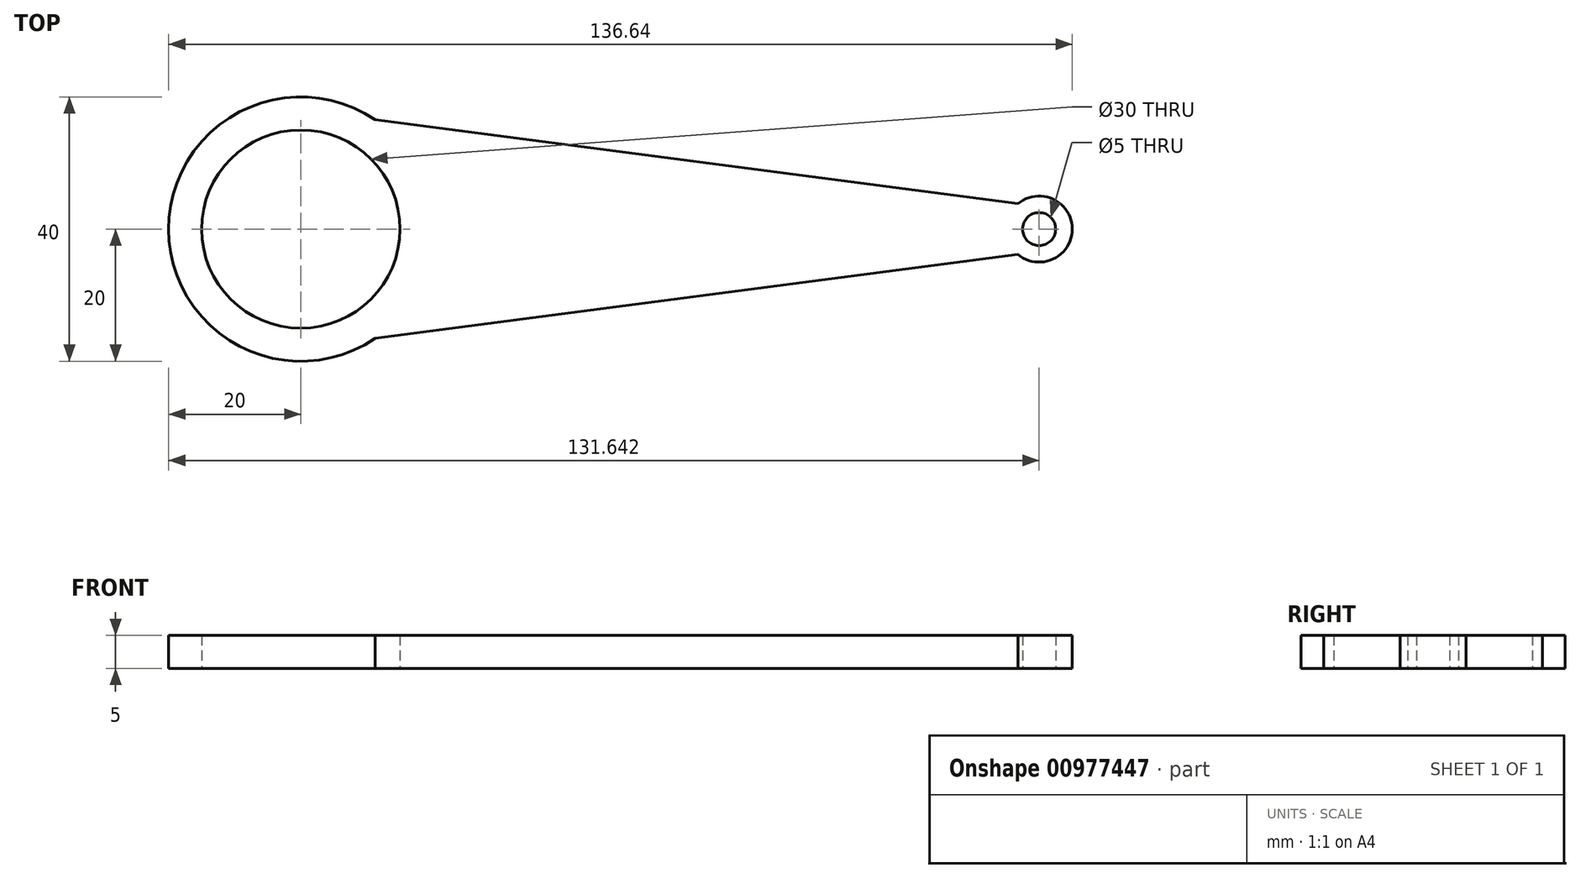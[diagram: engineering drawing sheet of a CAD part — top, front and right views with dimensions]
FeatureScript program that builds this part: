
annotation { "Feature Type Name" : "Feature", "Feature Type Description" : "" }
export const myFeature = defineFeature(function(context is Context, id is Id, definition is map)
    precondition{}
    {
        {
            var Q0;
            Q0=qCreatedBy(makeId("Top.planeOp"),FACE);
            var sketch = newSketch(context, id + "F0", { "sketchPlane" : qUnion([Q0])});
            skCircle(sketch, "E0", {"center": v(-131.43, 0) * mm, "radius": 15 * mm});
            skCircle(sketch, "E1", {"center": v(-19.79, 0) * mm, "radius": 2.5 * mm});
            skCircle(sketch, "E2", {"center": v(-131.43, 0) * mm, "radius": 20 * mm});
            skCircle(sketch, "E3", {"center": v(-19.79, 0) * mm, "radius": 5 * mm});
            skLineSegment(sketch, "E4", {"start": v(-131.43, 0) * mm, "end": v(-19.79, 0) * mm, "construction": true});
            skLineSegment(sketch, "E5", {"start": v(-120.18, 32.86) * mm, "end": v(-120.18, -33.62) * mm, "construction": true});
            skLineSegment(sketch, "E6", {"start": v(-22.99, 9.9) * mm, "end": v(-22.99, -15.53) * mm, "construction": true});
            skLineSegment(sketch, "E7", {"start": v(-120.18, 16.53) * mm, "end": v(-22.99, 3.84) * mm});
            skLineSegment(sketch, "E8", {"start": v(-22.99, -3.84) * mm, "end": v(-120.18, -16.53) * mm});
            skSolve(sketch);
        }
        {
            var Q0;
            Q0=makeQuery(id+"F0.imprint","IMPRINT",FACE,{"disambiguationData":[TD([[makeQuery(id+"F0.imprint","IMPRINT",EDGE,{"derivedFrom":sQuery(id+"F0.wireOp",EDGE,"E0")}),-1.0]])]});
            var Q1;
            {var subQ0=sQuery(id+"F0.wireOp",EDGE,"E7");Q1=makeQuery(id+"F0.imprint","IMPRINT",FACE,{"disambiguationData":[TD([[makeQuery(id+"F0.imprint","IMPRINT",EDGE,{"derivedFrom":subQ0}),-1.0]])]});}
            var Q2;
            Q2=makeQuery(id+"F0.imprint","IMPRINT",FACE,{"disambiguationData":[TD([[makeQuery(id+"F0.imprint","IMPRINT",EDGE,{"derivedFrom":sQuery(id+"F0.wireOp",EDGE,"E1")}),-1.0]])]});
            extrude(context, id + "F1", {"entities" : qUnion([Q0, Q1, Q2]), "depth" : 5 * mm, "offsetDistance" : 25 * mm});
        }
    });
